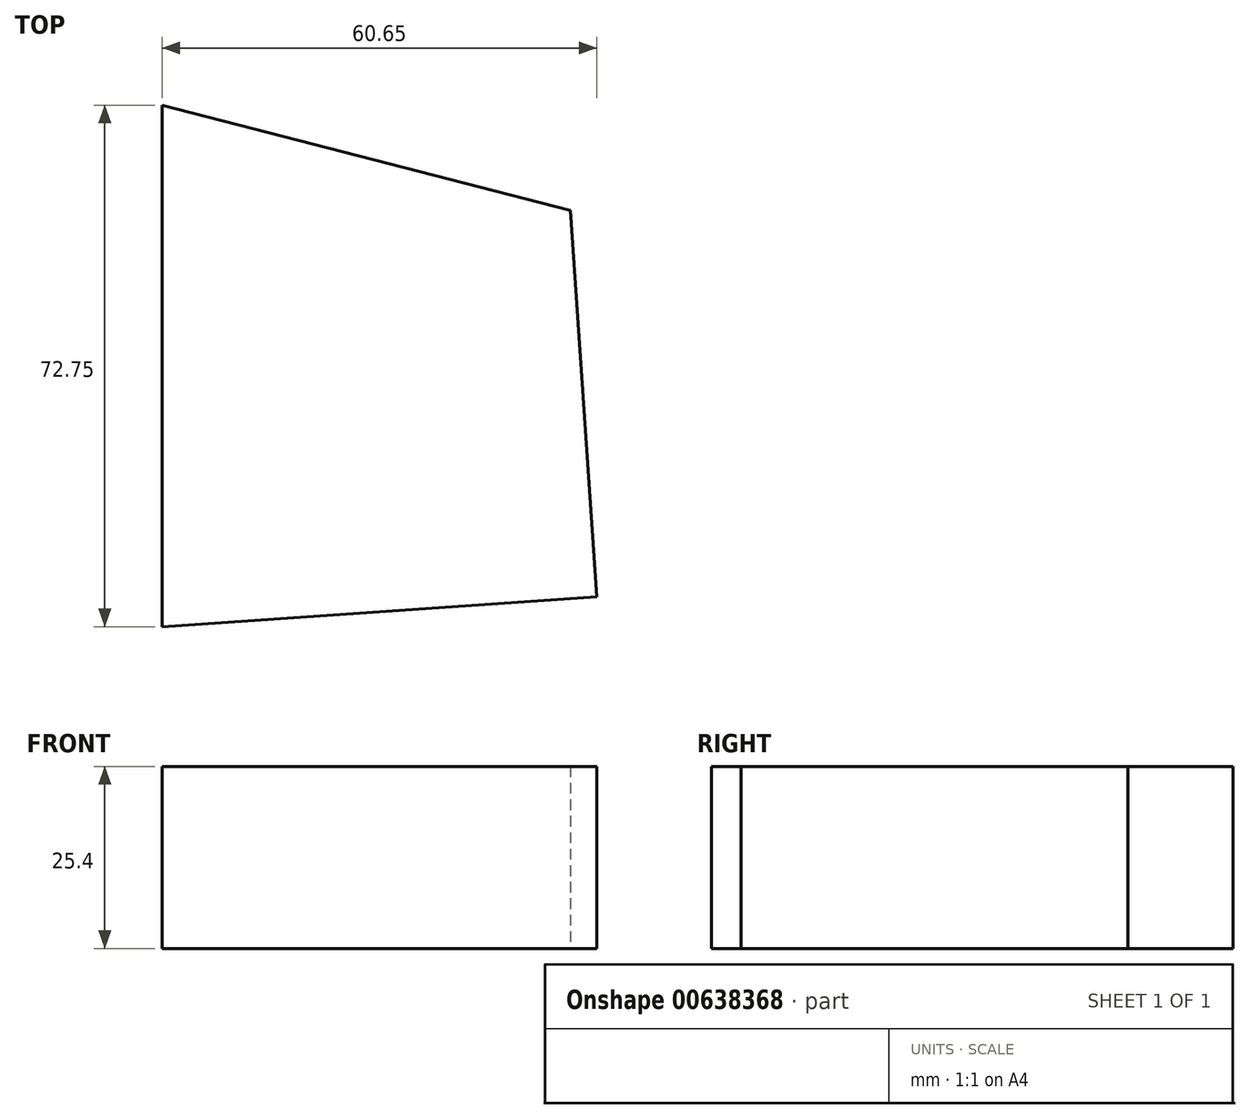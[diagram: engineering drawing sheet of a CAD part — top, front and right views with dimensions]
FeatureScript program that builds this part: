
annotation { "Feature Type Name" : "Feature", "Feature Type Description" : "" }
export const myFeature = defineFeature(function(context is Context, id is Id, definition is map)
    precondition{}
    {
        {
            var Q0;
            Q0=qCreatedBy(makeId("Top.planeOp"),FACE);
            var sketch = newSketch(context, id + "F0", { "sketchPlane" : qUnion([Q0])});
            skLineSegment(sketch, "E0", {"start": v(-31.34, 36.62) * mm, "end": v(-31.34, -36.13) * mm});
            skLineSegment(sketch, "E1", {"start": v(-31.34, -36.13) * mm, "end": v(29.3, -31.97) * mm});
            skLineSegment(sketch, "E2", {"start": v(29.3, -31.97) * mm, "end": v(25.6, 21.97) * mm});
            skLineSegment(sketch, "E3", {"start": v(25.6, 21.97) * mm, "end": v(-31.34, 36.62) * mm});
            skSolve(sketch);
        }
        {
            var Q0;
            Q0 = qSketchRegion(id + "F0", true);
            extrude(context, id + "F1", {"entities" : qUnion([Q0]), "depth" : 25.4 * mm, "offsetDistance" : 25.4 * mm});
        }
    });
